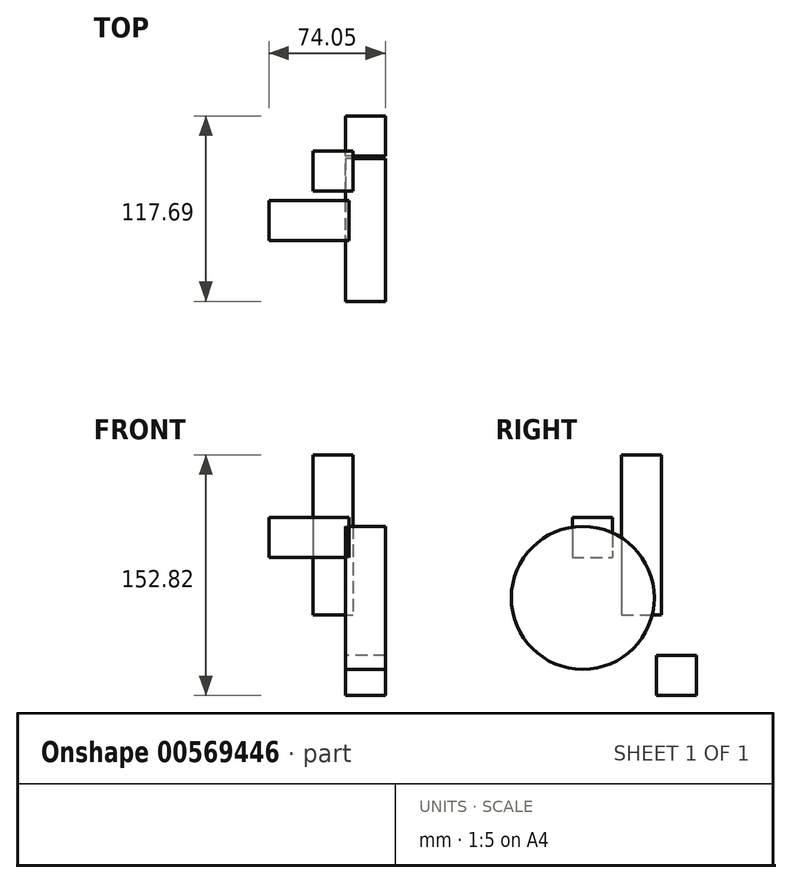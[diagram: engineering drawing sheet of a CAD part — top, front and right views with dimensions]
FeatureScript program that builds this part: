
annotation { "Feature Type Name" : "Feature", "Feature Type Description" : "" }
export const myFeature = defineFeature(function(context is Context, id is Id, definition is map)
    precondition{}
    {
        {
            var Q0;
            Q0=qCreatedBy(makeId("Front.planeOp"),FACE);
            var sketch = newSketch(context, id + "F0", { "sketchPlane" : qUnion([Q0])});
            skLineSegment(sketch, "E0.bottom", {"start": v(-48.65, 61.74) * mm, "end": v(2.15, 61.74) * mm});
            skLineSegment(sketch, "E0.top", {"start": v(-48.65, 36.34) * mm, "end": v(2.15, 36.34) * mm});
            skLineSegment(sketch, "E0.left", {"start": v(-48.65, 61.74) * mm, "end": v(-48.65, 36.34) * mm});
            skLineSegment(sketch, "E0.right", {"start": v(2.15, 61.74) * mm, "end": v(2.15, 36.34) * mm});
            skSolve(sketch);
        }
        {
            var Q0;
            Q0=makeQuery(id+"F0.imprint","IMPRINT",FACE,{"disambiguationData":[TD([[makeQuery(id+"F0.imprint","IMPRINT",EDGE,{"derivedFrom":sQuery(id+"F0.wireOp",EDGE,"E0.bottom")}),-1.0]])]});
            extrude(context, id + "F1", {"entities" : qUnion([Q0]), "depth" : 25.4 * mm, "offsetDistance" : 25.4 * mm});
        }
        {
            var Q0;
            Q0=qCreatedBy(makeId("Top.planeOp"),FACE);
            var sketch = newSketch(context, id + "F2", { "sketchPlane" : qUnion([Q0])});
            skLineSegment(sketch, "E1.bottom", {"start": v(-20.7, 5.86) * mm, "end": v(4.7, 5.86) * mm});
            skLineSegment(sketch, "E1.top", {"start": v(-20.7, 31.26) * mm, "end": v(4.7, 31.26) * mm});
            skLineSegment(sketch, "E1.left", {"start": v(-20.7, 5.86) * mm, "end": v(-20.7, 31.26) * mm});
            skLineSegment(sketch, "E1.right", {"start": v(4.7, 5.86) * mm, "end": v(4.7, 31.26) * mm});
            skSolve(sketch);
        }
        {
            var Q0;
            Q0=makeQuery(id+"F2.imprint","IMPRINT",FACE,{"disambiguationData":[TD([[makeQuery(id+"F2.imprint","IMPRINT",EDGE,{"derivedFrom":sQuery(id+"F2.wireOp",EDGE,"E1.bottom")}),1.0]])]});
            extrude(context, id + "F3", {"entities" : qUnion([Q0]), "depth" : 101.6 * mm, "offsetDistance" : 25.4 * mm});
        }
        {
            var Q0;
            Q0=qCreatedBy(makeId("Right.planeOp"),FACE);
            var sketch = newSketch(context, id + "F4", { "sketchPlane" : qUnion([Q0])});
            skLineSegment(sketch, "E2.bottom", {"start": v(28.12, -25.82) * mm, "end": v(53.52, -25.82) * mm});
            skLineSegment(sketch, "E2.top", {"start": v(28.12, -51.22) * mm, "end": v(53.52, -51.22) * mm});
            skLineSegment(sketch, "E2.left", {"start": v(28.12, -25.82) * mm, "end": v(28.12, -51.22) * mm});
            skLineSegment(sketch, "E2.right", {"start": v(53.52, -25.82) * mm, "end": v(53.52, -51.22) * mm});
            skSolve(sketch);
        }
        {
            var Q0;
            Q0 = qSketchRegion(id + "F4", true);
            extrude(context, id + "F5", {"entities" : qUnion([Q0]), "depth" : 25.4 * mm, "offsetDistance" : 25.4 * mm});
        }
        {
            var Q0;
            Q0 = qSketchRegion(id + "F2", true);
            extrude(context, id + "F6", {"entities" : qUnion([Q0]), "operationType" : NewBodyOperationType.ADD, "depth" : 25.4 * mm, "offsetDistance" : 25.4 * mm});
        }
        {
            var Q0;
            Q0=qCreatedBy(makeId("Right.planeOp"),FACE);
            var sketch = newSketch(context, id + "F7", { "sketchPlane" : qUnion([Q0])});
            skCircle(sketch, "E3", {"center": v(-18.8, 10.75) * mm, "radius": 45.37 * mm});
            skSolve(sketch);
        }
        {
            var Q0;
            Q0 = qSketchRegion(id + "F7", true);
            extrude(context, id + "F8", {"entities" : qUnion([Q0]), "depth" : 25.4 * mm, "offsetDistance" : 25.4 * mm});
        }
    });
